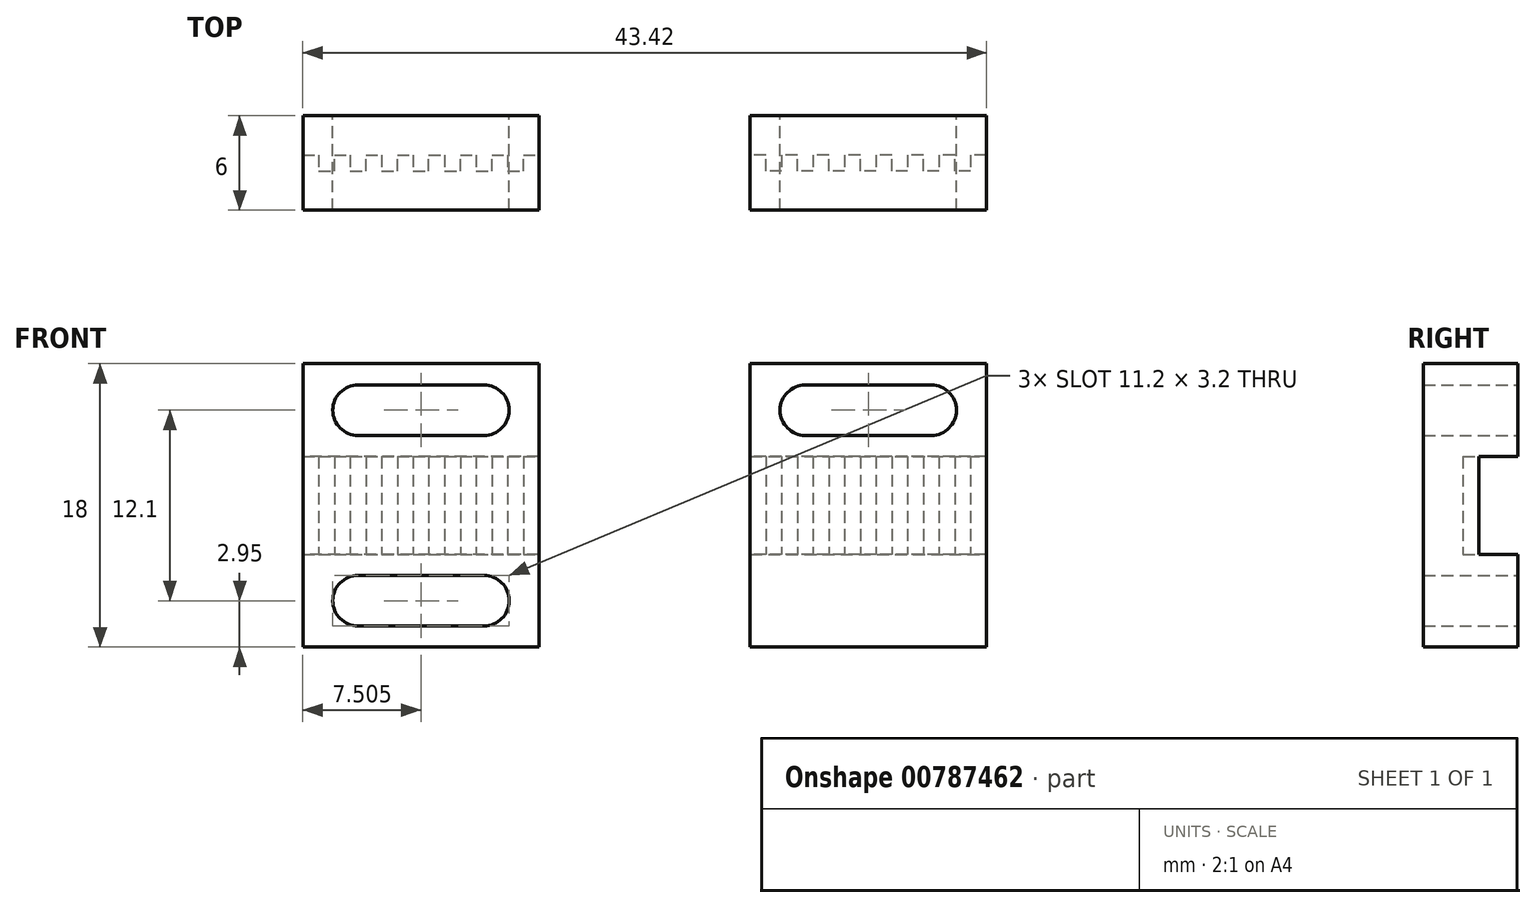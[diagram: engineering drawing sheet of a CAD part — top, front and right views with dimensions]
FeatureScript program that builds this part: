
annotation { "Feature Type Name" : "Feature", "Feature Type Description" : "" }
export const myFeature = defineFeature(function(context is Context, id is Id, definition is map)
    precondition{}
    {
        {
            var Q0;
            Q0=qCreatedBy(makeId("Top.planeOp"),FACE);
            var sketch = newSketch(context, id + "F0", { "sketchPlane" : qUnion([Q0])});
            skLineSegment(sketch, "E0", {"start": v(-27.25, 0) * mm, "end": v(25.91, 0) * mm, "construction": true});
            skLineSegment(sketch, "E1", {"start": v(0, 21.09) * mm, "end": v(0, -15.96) * mm, "construction": true});
            skLineSegment(sketch, "E2", {"start": v(-21.7, 0) * mm, "end": v(-21.7, 3.5) * mm});
            skLineSegment(sketch, "E3", {"start": v(-21.7, 3.5) * mm, "end": v(-20.7, 3.5) * mm});
            skLineSegment(sketch, "E4", {"start": v(-20.7, 3.5) * mm, "end": v(-20.7, 2.5) * mm});
            skLineSegment(sketch, "E5", {"start": v(-20.7, 2.5) * mm, "end": v(-19.7, 2.5) * mm});
            skLineSegment(sketch, "E6", {"start": v(-19.7, 2.5) * mm, "end": v(-19.7, 3.5) * mm});
            skLineSegment(sketch, "E7.1.0.0", {"start": v(-19.7, 3.5) * mm, "end": v(-18.7, 3.5) * mm});
            skLineSegment(sketch, "E7.1.0.1", {"start": v(-18.7, 3.5) * mm, "end": v(-18.7, 2.5) * mm});
            skLineSegment(sketch, "E7.1.0.2", {"start": v(-18.7, 2.5) * mm, "end": v(-17.7, 2.5) * mm});
            skLineSegment(sketch, "E7.1.0.3", {"start": v(-17.7, 2.5) * mm, "end": v(-17.7, 3.5) * mm});
            skLineSegment(sketch, "E7.2.0.0", {"start": v(-17.7, 3.5) * mm, "end": v(-16.7, 3.5) * mm});
            skLineSegment(sketch, "E7.2.0.1", {"start": v(-16.7, 3.5) * mm, "end": v(-16.7, 2.5) * mm});
            skLineSegment(sketch, "E7.2.0.2", {"start": v(-16.7, 2.5) * mm, "end": v(-15.7, 2.5) * mm});
            skLineSegment(sketch, "E7.2.0.3", {"start": v(-15.7, 2.5) * mm, "end": v(-15.7, 3.5) * mm});
            skLineSegment(sketch, "E7.3.0.0", {"start": v(-15.7, 3.5) * mm, "end": v(-14.7, 3.5) * mm});
            skLineSegment(sketch, "E7.3.0.1", {"start": v(-14.7, 3.5) * mm, "end": v(-14.7, 2.5) * mm});
            skLineSegment(sketch, "E7.3.0.2", {"start": v(-14.7, 2.5) * mm, "end": v(-13.7, 2.5) * mm});
            skLineSegment(sketch, "E7.3.0.3", {"start": v(-13.7, 2.5) * mm, "end": v(-13.7, 3.5) * mm});
            skLineSegment(sketch, "E7.4.0.0", {"start": v(-13.7, 3.5) * mm, "end": v(-12.7, 3.5) * mm});
            skLineSegment(sketch, "E7.4.0.1", {"start": v(-12.7, 3.5) * mm, "end": v(-12.7, 2.5) * mm});
            skLineSegment(sketch, "E7.4.0.2", {"start": v(-12.7, 2.5) * mm, "end": v(-11.7, 2.5) * mm});
            skLineSegment(sketch, "E7.4.0.3", {"start": v(-11.7, 2.5) * mm, "end": v(-11.7, 3.5) * mm});
            skLineSegment(sketch, "E7.5.0.0", {"start": v(-11.7, 3.5) * mm, "end": v(-10.7, 3.5) * mm});
            skLineSegment(sketch, "E7.5.0.1", {"start": v(-10.7, 3.5) * mm, "end": v(-10.7, 2.5) * mm});
            skLineSegment(sketch, "E7.5.0.2", {"start": v(-10.7, 2.5) * mm, "end": v(-9.7, 2.5) * mm});
            skLineSegment(sketch, "E7.5.0.3", {"start": v(-9.7, 2.5) * mm, "end": v(-9.7, 3.5) * mm});
            skLineSegment(sketch, "E7.6.0.0", {"start": v(-9.7, 3.5) * mm, "end": v(-8.7, 3.5) * mm});
            skLineSegment(sketch, "E7.6.0.1", {"start": v(-8.7, 3.5) * mm, "end": v(-8.7, 2.5) * mm});
            skLineSegment(sketch, "E7.6.0.2", {"start": v(-8.7, 2.5) * mm, "end": v(-7.7, 2.5) * mm});
            skLineSegment(sketch, "E7.6.0.3", {"start": v(-7.7, 2.5) * mm, "end": v(-7.7, 3.5) * mm});
            skLineSegment(sketch, "E7.7.0.0", {"start": v(-7.7, 3.5) * mm, "end": v(-6.7, 3.5) * mm});
            skLineSegment(sketch, "E7.7.0.1", {"start": v(-6.7, 3.5) * mm, "end": v(-6.7, 2.5) * mm});
            skLineSegment(sketch, "E7.direction1", {"start": v(-21.7, 3.5) * mm, "end": v(-19.7, 3.5) * mm, "construction": true});
            skLineSegment(sketch, "E8", {"start": v(-6.7, 2.5) * mm, "end": v(-6.7, 0) * mm});
            skLineSegment(sketch, "E9", {"start": v(-6.7, 0) * mm, "end": v(-21.7, 0) * mm});
            skLineSegment(sketch, "E10.MirrorCS", {"start": v(9.7, 2.5) * mm, "end": v(9.7, 3.5) * mm});
            skLineSegment(sketch, "E11.MirrorCS", {"start": v(8.7, 3.5) * mm, "end": v(8.7, 2.5) * mm});
            skLineSegment(sketch, "E12.MirrorCS", {"start": v(8.7, 2.5) * mm, "end": v(7.7, 2.5) * mm});
            skLineSegment(sketch, "E13.MirrorCS", {"start": v(9.7, 3.5) * mm, "end": v(8.7, 3.5) * mm});
            skLineSegment(sketch, "E14.MirrorCS", {"start": v(7.7, 2.5) * mm, "end": v(7.7, 3.5) * mm});
            skLineSegment(sketch, "E15.MirrorCS", {"start": v(17.7, 2.5) * mm, "end": v(17.7, 3.5) * mm});
            skLineSegment(sketch, "E16.MirrorCS", {"start": v(6.7, 3.5) * mm, "end": v(6.7, 2.5) * mm});
            skLineSegment(sketch, "E17.MirrorCS", {"start": v(16.7, 3.5) * mm, "end": v(16.7, 2.5) * mm});
            skLineSegment(sketch, "E18.MirrorCS", {"start": v(19.7, 2.5) * mm, "end": v(19.7, 3.5) * mm});
            skLineSegment(sketch, "E19.MirrorCS", {"start": v(15.7, 2.5) * mm, "end": v(15.7, 3.5) * mm});
            skLineSegment(sketch, "E20.MirrorCS", {"start": v(21.7, 3.5) * mm, "end": v(19.7, 3.5) * mm, "construction": true});
            skLineSegment(sketch, "E21.MirrorCS", {"start": v(18.7, 3.5) * mm, "end": v(18.7, 2.5) * mm});
            skLineSegment(sketch, "E22.MirrorCS", {"start": v(16.7, 2.5) * mm, "end": v(15.7, 2.5) * mm});
            skLineSegment(sketch, "E23.MirrorCS", {"start": v(19.7, 3.5) * mm, "end": v(18.7, 3.5) * mm});
            skLineSegment(sketch, "E24.MirrorCS", {"start": v(21.7, 3.5) * mm, "end": v(20.7, 3.5) * mm});
            skLineSegment(sketch, "E25.MirrorCS", {"start": v(10.7, 2.5) * mm, "end": v(9.7, 2.5) * mm});
            skLineSegment(sketch, "E26.MirrorCS", {"start": v(20.7, 3.5) * mm, "end": v(20.7, 2.5) * mm});
            skLineSegment(sketch, "E27.MirrorCS", {"start": v(13.7, 3.5) * mm, "end": v(12.7, 3.5) * mm});
            skLineSegment(sketch, "E28.MirrorCS", {"start": v(12.7, 3.5) * mm, "end": v(12.7, 2.5) * mm});
            skLineSegment(sketch, "E29.MirrorCS", {"start": v(10.7, 3.5) * mm, "end": v(10.7, 2.5) * mm});
            skLineSegment(sketch, "E30.MirrorCS", {"start": v(11.7, 2.5) * mm, "end": v(11.7, 3.5) * mm});
            skLineSegment(sketch, "E31.MirrorCS", {"start": v(12.7, 2.5) * mm, "end": v(11.7, 2.5) * mm});
            skLineSegment(sketch, "E32.MirrorCS", {"start": v(14.7, 3.5) * mm, "end": v(14.7, 2.5) * mm});
            skLineSegment(sketch, "E33.MirrorCS", {"start": v(14.7, 2.5) * mm, "end": v(13.7, 2.5) * mm});
            skLineSegment(sketch, "E34.MirrorCS", {"start": v(11.7, 3.5) * mm, "end": v(10.7, 3.5) * mm});
            skLineSegment(sketch, "E35.MirrorCS", {"start": v(7.7, 3.5) * mm, "end": v(6.7, 3.5) * mm});
            skLineSegment(sketch, "E36.MirrorCS", {"start": v(17.7, 3.5) * mm, "end": v(16.7, 3.5) * mm});
            skLineSegment(sketch, "E37.MirrorCS", {"start": v(18.7, 2.5) * mm, "end": v(17.7, 2.5) * mm});
            skLineSegment(sketch, "E38.MirrorCS", {"start": v(20.7, 2.5) * mm, "end": v(19.7, 2.5) * mm});
            skLineSegment(sketch, "E39.MirrorCS", {"start": v(13.7, 2.5) * mm, "end": v(13.7, 3.5) * mm});
            skLineSegment(sketch, "E40.MirrorCS", {"start": v(15.7, 3.5) * mm, "end": v(14.7, 3.5) * mm});
            skLineSegment(sketch, "E41.MirrorCS", {"start": v(6.7, 0) * mm, "end": v(21.7, 0) * mm});
            skLineSegment(sketch, "E42.MirrorCS", {"start": v(21.7, 0) * mm, "end": v(21.7, 3.5) * mm});
            skLineSegment(sketch, "E43.MirrorCS", {"start": v(27.25, 0) * mm, "end": v(-25.91, 0) * mm, "construction": true});
            skLineSegment(sketch, "E44.MirrorCS", {"start": v(6.7, 2.5) * mm, "end": v(6.7, 0) * mm});
            skSolve(sketch);
        }
        {
            var Q0;
            Q0=makeQuery(id+"F0.imprint","IMPRINT",FACE,{"disambiguationData":[TD([[makeQuery(id+"F0.imprint","IMPRINT",EDGE,{"derivedFrom":sQuery(id+"F0.wireOp",EDGE,"E2")}),-1.0]])]});
            extrude(context, id + "F1", {"entities" : qUnion([Q0]), "depth" : 3.1 * mm, "offsetDistance" : 25 * mm, "hasSecondDirection" : true, "secondDirectionOppositeDirection" : true, "secondDirectionDepth" : 3.1 * mm});
        }
        {
            var Q0;
            Q0=makeQuery(id+"F0.imprint","IMPRINT",FACE,{"disambiguationData":[TD([[makeQuery(id+"F0.imprint","IMPRINT",EDGE,{"derivedFrom":sQuery(id+"F0.wireOp",EDGE,"E10.MirrorCS")}),1.0]])]});
            extrude(context, id + "F2", {"entities" : qUnion([Q0]), "depth" : 3.1 * mm, "offsetDistance" : 25 * mm, "hasSecondDirection" : true, "secondDirectionOppositeDirection" : true, "secondDirectionDepth" : 3.1 * mm});
        }
        {
            var Q0;
            Q0=makeQuery(id+"F1.opExtrude","SWEPT_FACE",FACE,{"disambiguationData":[OSD([sQuery(id+"F0.wireOp",EDGE,"E9")])]});
            var sketch = newSketch(context, id + "F3", { "sketchPlane" : qUnion([Q0])});
            skLineSegment(sketch, "E45.bottom", {"start": v(-6.7, 9) * mm, "end": v(-21.7, 9) * mm});
            skLineSegment(sketch, "E45.top", {"start": v(-6.7, -9) * mm, "end": v(-21.7, -9) * mm});
            skLineSegment(sketch, "E45.left", {"start": v(-6.7, 9) * mm, "end": v(-6.7, 3.1) * mm});
            skLineSegment(sketch, "E45.right", {"start": v(-21.7, 9) * mm, "end": v(-21.7, 3.1) * mm});
            skLineSegment(sketch, "E46", {"start": v(-6.7, -3.1) * mm, "end": v(-21.7, -3.1) * mm});
            skLineSegment(sketch, "E47", {"start": v(-6.7, 3.1) * mm, "end": v(-21.7, 3.1) * mm});
            skLineSegment(sketch, "E48.trimOffspring", {"start": v(-6.7, -3.1) * mm, "end": v(-6.7, -9) * mm});
            skLineSegment(sketch, "E49.trimOffspring", {"start": v(-21.7, -3.1) * mm, "end": v(-21.7, -9) * mm});
            skLineSegment(sketch, "E50", {"start": v(0, -5.98) * mm, "end": v(0, 9.88) * mm, "construction": true});
            skLineSegment(sketch, "E51.MirrorCS", {"start": v(6.7, -3.1) * mm, "end": v(6.7, -9) * mm});
            skLineSegment(sketch, "E52.MirrorCS", {"start": v(21.7, -3.1) * mm, "end": v(21.7, -9) * mm});
            skLineSegment(sketch, "E53.MirrorCS", {"start": v(6.7, -3.1) * mm, "end": v(21.7, -3.1) * mm});
            skLineSegment(sketch, "E54.MirrorCS", {"start": v(6.7, 3.1) * mm, "end": v(21.7, 3.1) * mm});
            skLineSegment(sketch, "E55.MirrorCS", {"start": v(6.7, -9) * mm, "end": v(21.7, -9) * mm});
            skLineSegment(sketch, "E56.MirrorCS", {"start": v(21.7, 9) * mm, "end": v(21.7, 3.1) * mm});
            skLineSegment(sketch, "E57.MirrorCS", {"start": v(6.7, 9) * mm, "end": v(21.7, 9) * mm});
            skLineSegment(sketch, "E58.MirrorCS", {"start": v(6.7, 9) * mm, "end": v(6.7, 3.1) * mm});
            skSolve(sketch);
        }
        {
            var Q0;
            Q0=makeQuery(id+"F3.imprint","IMPRINT",FACE,{"disambiguationData":[TD([[makeQuery(id+"F3.imprint","IMPRINT",EDGE,{"derivedFrom":sQuery(id+"F3.wireOp",EDGE,"E51.MirrorCS")}),1.0]])]});
            var Q1;
            Q1=makeQuery(id+"F3.imprint","IMPRINT",FACE,{"disambiguationData":[TD([[makeQuery(id+"F3.imprint","IMPRINT",EDGE,{"derivedFrom":sQuery(id+"F3.wireOp",EDGE,"E54.MirrorCS")}),1.0]])]});
            extrude(context, id + "F4", {"entities" : qUnion([Q0, Q1]), "operationType" : NewBodyOperationType.ADD, "oppositeDirection" : true, "depth" : 6 * mm, "offsetDistance" : 25 * mm});
        }
        {
            var Q0;
            Q0=makeQuery(id+"F3.imprint","IMPRINT",FACE,{"disambiguationData":[TD([[makeQuery(id+"F3.imprint","IMPRINT",EDGE,{"derivedFrom":sQuery(id+"F3.wireOp",EDGE,"E45.top")}),-1.0]])]});
            var Q1;
            Q1=makeQuery(id+"F3.imprint","IMPRINT",FACE,{"disambiguationData":[TD([[makeQuery(id+"F3.imprint","IMPRINT",EDGE,{"derivedFrom":sQuery(id+"F3.wireOp",EDGE,"E45.bottom")}),1.0]])]});
            extrude(context, id + "F5", {"entities" : qUnion([Q0, Q1]), "operationType" : NewBodyOperationType.ADD, "oppositeDirection" : true, "depth" : 6 * mm, "offsetDistance" : 25 * mm});
        }
        {
            var Q0;
            Q0=makeQuery(id+"F5.opExtrude","CAP_FACE",FACE,{"disambiguationData":[OSD([sQuery(id+"F3.wireOp",EDGE,"E45.top"),sQuery(id+"F3.wireOp",EDGE,"E46"),sQuery(id+"F3.wireOp",EDGE,"E48.trimOffspring"),sQuery(id+"F3.wireOp",EDGE,"E49.trimOffspring")])],"isStart":false});
            var sketch = newSketch(context, id + "F6", { "sketchPlane" : qUnion([Q0])});
            skLineSegment(sketch, "E59", {"start": v(21.7, -6.05) * mm, "end": v(6.7, -6.05) * mm, "construction": true});
            skArc(sketch, "E60", {"start": v(18.2, -7.65) * mm, "mid": v(19.8, -6.05) * mm, "end": v(18.2, -4.45) * mm});
            skArc(sketch, "E61", {"start": v(10.2, -4.45) * mm, "mid": v(8.6, -6.05) * mm, "end": v(10.2, -7.65) * mm});
            skLineSegment(sketch, "E62", {"start": v(18.2, -7.65) * mm, "end": v(10.2, -7.65) * mm});
            skLineSegment(sketch, "E63", {"start": v(18.2, -4.45) * mm, "end": v(10.2, -4.45) * mm});
            skArc(sketch, "E64.MirrorCS", {"start": v(-10.2, -4.45) * mm, "mid": v(-8.6, -6.05) * mm, "end": v(-10.2, -7.65) * mm});
            skLineSegment(sketch, "E65.MirrorCS", {"start": v(-18.2, -7.65) * mm, "end": v(-10.2, -7.65) * mm});
            skArc(sketch, "E66.MirrorCS", {"start": v(-18.2, -7.65) * mm, "mid": v(-19.8, -6.05) * mm, "end": v(-18.2, -4.45) * mm});
            skLineSegment(sketch, "E67.MirrorCS", {"start": v(-18.2, -4.45) * mm, "end": v(-10.2, -4.45) * mm});
            skLineSegment(sketch, "E68.MirrorCS", {"start": v(18.2, 4.45) * mm, "end": v(10.2, 4.45) * mm});
            skArc(sketch, "E69.MirrorCS", {"start": v(10.2, 4.45) * mm, "mid": v(8.6, 6.05) * mm, "end": v(10.2, 7.65) * mm});
            skLineSegment(sketch, "E70.MirrorCS", {"start": v(18.2, 7.65) * mm, "end": v(10.2, 7.65) * mm});
            skArc(sketch, "E71.MirrorCS", {"start": v(18.2, 7.65) * mm, "mid": v(19.8, 6.05) * mm, "end": v(18.2, 4.45) * mm});
            skLineSegment(sketch, "E72.MirrorCS", {"start": v(-18.2, 4.45) * mm, "end": v(-10.2, 4.45) * mm});
            skArc(sketch, "E73.MirrorCS", {"start": v(-10.2, 4.45) * mm, "mid": v(-8.6, 6.05) * mm, "end": v(-10.2, 7.65) * mm});
            skLineSegment(sketch, "E74.MirrorCS", {"start": v(-18.2, 7.65) * mm, "end": v(-10.2, 7.65) * mm});
            skArc(sketch, "E75.MirrorCS", {"start": v(-18.2, 7.65) * mm, "mid": v(-19.8, 6.05) * mm, "end": v(-18.2, 4.45) * mm});
            skSolve(sketch);
        }
        {
            var Q0;
            Q0=makeQuery(id+"F6.imprint","IMPRINT",FACE,{"disambiguationData":[TD([[makeQuery(id+"F6.imprint","IMPRINT",EDGE,{"derivedFrom":sQuery(id+"F6.wireOp",EDGE,"E60")}),1.0]])]});
            var Q1;
            Q1=makeQuery(id+"F6.imprint","IMPRINT",FACE,{"disambiguationData":[TD([[makeQuery(id+"F6.imprint","IMPRINT",EDGE,{"derivedFrom":sQuery(id+"F6.wireOp",EDGE,"E68.MirrorCS")}),-1.0]])]});
            extrude(context, id + "F7", {"entities" : qUnion([Q0, Q1]), "operationType" : NewBodyOperationType.REMOVE, "endBound" : BoundingType.UP_TO_NEXT, "oppositeDirection" : true, "depth" : 25 * mm, "offsetDistance" : 25 * mm});
        }
        {
            var Q0;
            Q0=makeQuery(id+"F6.imprint","IMPRINT",FACE,{"disambiguationData":[TD([[makeQuery(id+"F6.imprint","IMPRINT",EDGE,{"derivedFrom":sQuery(id+"F6.wireOp",EDGE,"E64.MirrorCS")}),-1.0]])]});
            var Q1;
            Q1=makeQuery(id+"F6.imprint","IMPRINT",FACE,{"disambiguationData":[TD([[makeQuery(id+"F6.imprint","IMPRINT",EDGE,{"derivedFrom":sQuery(id+"F6.wireOp",EDGE,"E72.MirrorCS")}),1.0]])]});
            extrude(context, id + "F8", {"entities" : qUnion([Q0, Q1]), "operationType" : NewBodyOperationType.REMOVE, "endBound" : BoundingType.UP_TO_NEXT, "oppositeDirection" : true, "depth" : 25 * mm, "offsetDistance" : 25 * mm});
        }
    });
